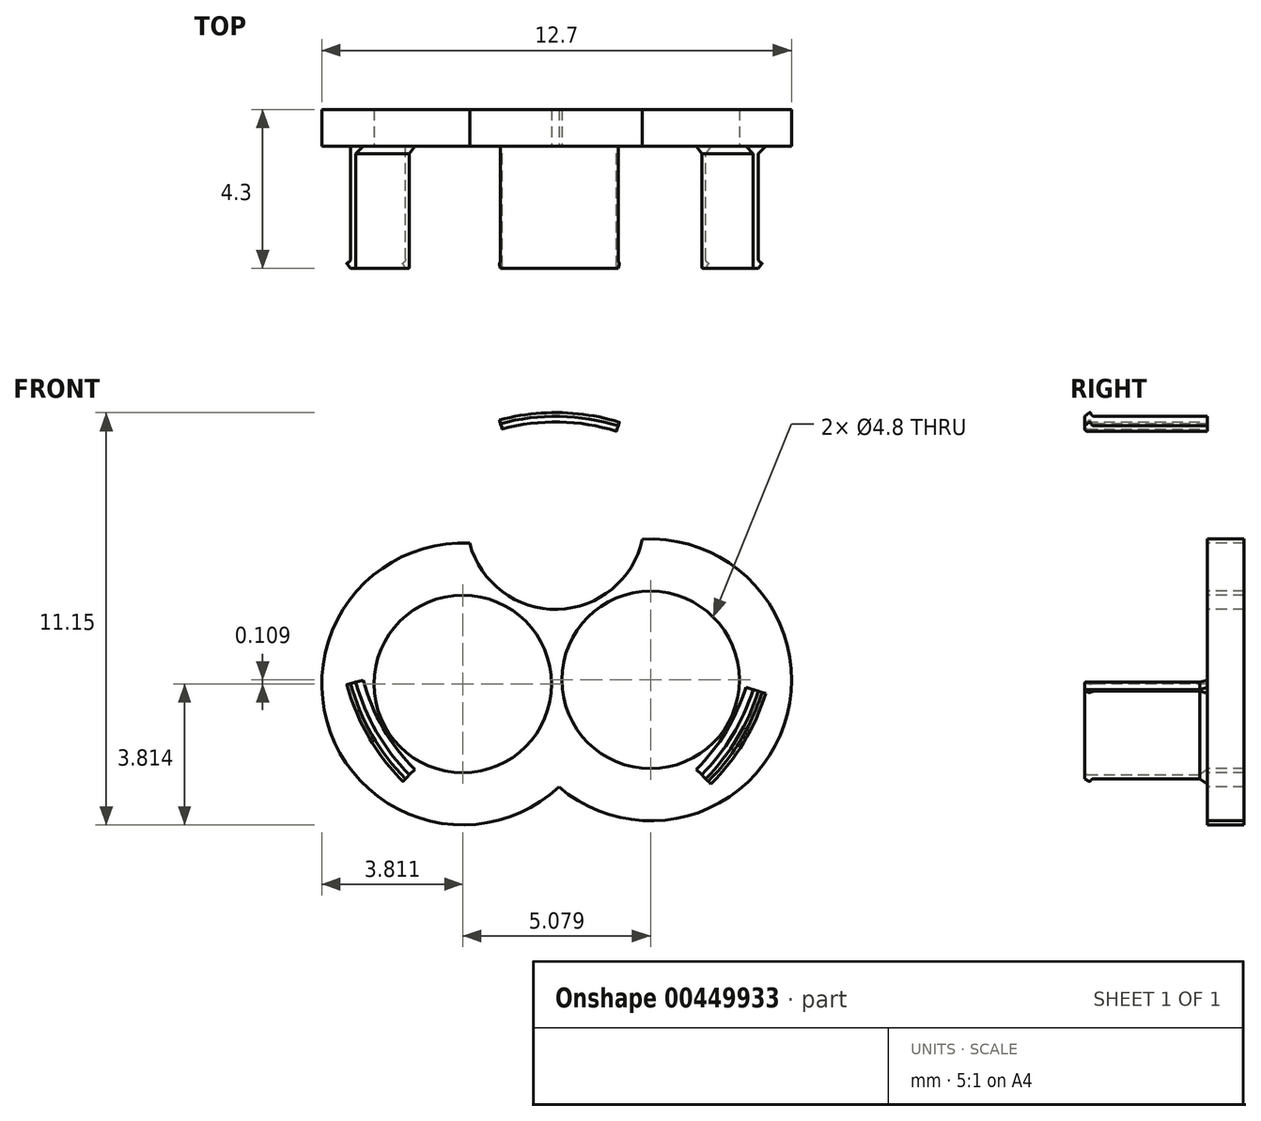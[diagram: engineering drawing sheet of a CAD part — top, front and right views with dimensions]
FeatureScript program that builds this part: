
annotation { "Feature Type Name" : "Feature", "Feature Type Description" : "" }
export const myFeature = defineFeature(function(context is Context, id is Id, definition is map)
    precondition{}
    {
        {
            var Q0;
            Q0=qCreatedBy(makeId("Front.planeOp"),FACE);
            var sketch = newSketch(context, id + "F0", { "sketchPlane" : qUnion([Q0])});
            skCircle(sketch, "E0", {"center": v(-2.5, -1.5) * mm, "radius": 2.4 * mm});
            skCircle(sketch, "E1", {"center": v(0, 2.92) * mm, "radius": 2.4 * mm});
            skCircle(sketch, "E2", {"center": v(0, 0) * mm, "radius": 2.92 * mm});
            skCircle(sketch, "E3", {"center": v(2.57, -1.39) * mm, "radius": 2.4 * mm});
            skCircle(sketch, "E4", {"center": v(-2.5, -1.5) * mm, "radius": 3.81 * mm});
            skCircle(sketch, "E5", {"center": v(0, 2.92) * mm, "radius": 3.81 * mm});
            skCircle(sketch, "E6", {"center": v(2.57, -1.39) * mm, "radius": 3.81 * mm});
            skSolve(sketch);
        }
        {
            var Q0;
            {var subQ0=sQuery(id+"F0.wireOp",EDGE,"E2");var subQ1=sQuery(id+"F0.wireOp",EDGE,"E0");var subQ2=makeQuery(id+"F0.imprint","INTERSECT",VERTEX,{"disambiguationData":[OD(0.0)],"derivedFrom":[subQ1,subQ0]});Q0=makeQuery(id+"F0.imprint","IMPRINT",FACE,{"disambiguationData":[TD([[makeQuery(id+"F0.imprint","IMPRINT",EDGE,{"disambiguationData":[TD([[subQ2,-1.0]])],"derivedFrom":subQ1}),-1.0]])]});}
            var Q1;
            {var subQ1=sQuery(id+"F0.wireOp",EDGE,"E2");var subQ5=sQuery(id+"F0.wireOp",EDGE,"E1");var subQ6=makeQuery(id+"F0.imprint","INTERSECT",VERTEX,{"disambiguationData":[OD(0.0)],"derivedFrom":[subQ5,subQ1]});Q1=makeQuery(id+"F0.imprint","IMPRINT",FACE,{"disambiguationData":[TD([[makeQuery(id+"F0.imprint","IMPRINT",EDGE,{"disambiguationData":[TD([[subQ6,-1.0]])],"derivedFrom":subQ5}),-1.0]])]});}
            var Q2;
            {var subQ5=sQuery(id+"F0.wireOp",EDGE,"E2");var subQ7=sQuery(id+"F0.wireOp",EDGE,"E1");var subQ9=makeQuery(id+"F0.imprint","INTERSECT",VERTEX,{"disambiguationData":[OD(0.0)],"derivedFrom":[subQ7,subQ5]});Q2=makeQuery(id+"F0.imprint","IMPRINT",FACE,{"disambiguationData":[TD([[makeQuery(id+"F0.imprint","IMPRINT",EDGE,{"disambiguationData":[TD([[subQ9,1.0]])],"derivedFrom":subQ7}),-1.0]])]});}
            var Q3;
            {var subQ1=sQuery(id+"F0.wireOp",EDGE,"E2");var subQ3=sQuery(id+"F0.wireOp",EDGE,"E0");var subQ5=makeQuery(id+"F0.imprint","INTERSECT",VERTEX,{"disambiguationData":[OD(0.0)],"derivedFrom":[subQ3,subQ1]});Q3=makeQuery(id+"F0.imprint","IMPRINT",FACE,{"disambiguationData":[TD([[makeQuery(id+"F0.imprint","IMPRINT",EDGE,{"disambiguationData":[TD([[subQ5,1.0]])],"derivedFrom":subQ3}),-1.0]])]});}
            var Q4;
            {var subQ0=sQuery(id+"F0.wireOp",EDGE,"E5");var subQ1=sQuery(id+"F0.wireOp",EDGE,"E0");var subQ2=makeQuery(id+"F0.imprint","INTERSECT",VERTEX,{"disambiguationData":[OD(1.0)],"derivedFrom":[subQ1,subQ0]});Q4=makeQuery(id+"F0.imprint","IMPRINT",FACE,{"disambiguationData":[TD([[makeQuery(id+"F0.imprint","IMPRINT",EDGE,{"disambiguationData":[TD([[subQ2,-1.0]])],"derivedFrom":subQ1}),-1.0]])]});}
            var Q5;
            {var subQ0=sQuery(id+"F0.wireOp",EDGE,"E6");var subQ5=sQuery(id+"F0.wireOp",EDGE,"E0");var subQ6=makeQuery(id+"F0.imprint","INTERSECT",VERTEX,{"disambiguationData":[OD(1.0)],"derivedFrom":[subQ5,subQ0]});Q5=makeQuery(id+"F0.imprint","IMPRINT",FACE,{"disambiguationData":[TD([[makeQuery(id+"F0.imprint","IMPRINT",EDGE,{"disambiguationData":[TD([[subQ6,-1.0]])],"derivedFrom":subQ5}),-1.0]])]});}
            var Q6;
            {var subQ0=sQuery(id+"F0.wireOp",EDGE,"E5");var subQ1=sQuery(id+"F0.wireOp",EDGE,"E3");var subQ2=makeQuery(id+"F0.imprint","INTERSECT",VERTEX,{"disambiguationData":[OD(0.0)],"derivedFrom":[subQ1,subQ0]});Q6=makeQuery(id+"F0.imprint","IMPRINT",FACE,{"disambiguationData":[TD([[makeQuery(id+"F0.imprint","IMPRINT",EDGE,{"disambiguationData":[TD([[subQ2,1.0]])],"derivedFrom":subQ1}),-1.0]])]});}
            var Q7;
            {var subQ0=sQuery(id+"F0.wireOp",EDGE,"E5");var subQ1=sQuery(id+"F0.wireOp",EDGE,"E0");var subQ2=makeQuery(id+"F0.imprint","INTERSECT",VERTEX,{"disambiguationData":[OD(0.0)],"derivedFrom":[subQ1,subQ0]});Q7=makeQuery(id+"F0.imprint","IMPRINT",FACE,{"disambiguationData":[TD([[makeQuery(id+"F0.imprint","IMPRINT",EDGE,{"disambiguationData":[TD([[subQ2,1.0]])],"derivedFrom":subQ1}),-1.0]])]});}
            var Q8;
            {var subQ7=sQuery(id+"F0.wireOp",EDGE,"E6");var subQ9=sQuery(id+"F0.wireOp",EDGE,"E0");var subQ10=makeQuery(id+"F0.imprint","INTERSECT",VERTEX,{"disambiguationData":[OD(0.0)],"derivedFrom":[subQ9,subQ7]});Q8=makeQuery(id+"F0.imprint","IMPRINT",FACE,{"disambiguationData":[TD([[makeQuery(id+"F0.imprint","IMPRINT",EDGE,{"disambiguationData":[TD([[subQ10,1.0]])],"derivedFrom":subQ9}),-1.0]])]});}
            var Q9;
            {var subQ1=sQuery(id+"F0.wireOp",EDGE,"E2");var subQ5=sQuery(id+"F0.wireOp",EDGE,"E1");var subQ6=makeQuery(id+"F0.imprint","INTERSECT",VERTEX,{"disambiguationData":[OD(1.0)],"derivedFrom":[subQ5,subQ1]});Q9=makeQuery(id+"F0.imprint","IMPRINT",FACE,{"disambiguationData":[TD([[makeQuery(id+"F0.imprint","IMPRINT",EDGE,{"disambiguationData":[TD([[subQ6,-1.0]])],"derivedFrom":subQ5}),-1.0]])]});}
            var Q10;
            {var subQ0=sQuery(id+"F0.wireOp",EDGE,"E4");var subQ1=sQuery(id+"F0.wireOp",EDGE,"E1");var subQ2=makeQuery(id+"F0.imprint","INTERSECT",VERTEX,{"disambiguationData":[OD(1.0)],"derivedFrom":[subQ1,subQ0]});Q10=makeQuery(id+"F0.imprint","IMPRINT",FACE,{"disambiguationData":[TD([[makeQuery(id+"F0.imprint","IMPRINT",EDGE,{"disambiguationData":[TD([[subQ2,-1.0]])],"derivedFrom":subQ1}),-1.0]])]});}
            var Q11;
            {var subQ0=sQuery(id+"F0.wireOp",EDGE,"E4");var subQ1=sQuery(id+"F0.wireOp",EDGE,"E1");var subQ2=makeQuery(id+"F0.imprint","INTERSECT",VERTEX,{"disambiguationData":[OD(0.0)],"derivedFrom":[subQ1,subQ0]});Q11=makeQuery(id+"F0.imprint","IMPRINT",FACE,{"disambiguationData":[TD([[makeQuery(id+"F0.imprint","IMPRINT",EDGE,{"disambiguationData":[TD([[subQ2,1.0]])],"derivedFrom":subQ1}),-1.0]])]});}
            extrude(context, id + "F1", {"entities" : qUnion([Q0, Q1, Q2, Q3, Q4, Q5, Q6, Q7, Q8, Q9, Q10, Q11]), "oppositeDirection" : true, "depth" : 1 * mm});
        }
        {
            var Q0;
            Q0=qCreatedBy(makeId("Right.planeOp"),FACE);
            var sketch = newSketch(context, id + "F2", { "sketchPlane" : qUnion([Q0])});
            skLineSegment(sketch, "E7", {"start": v(0, 5.59) * mm, "end": v(-3.25, 5.59) * mm});
            skLineSegment(sketch, "E8", {"start": v(-3.3, 5.64) * mm, "end": v(-3.3, 5.74) * mm});
            skLineSegment(sketch, "E9", {"start": v(-3.3, 5.74) * mm, "end": v(-3.15, 5.87) * mm});
            skLineSegment(sketch, "E10", {"start": v(-3.15, 5.87) * mm, "end": v(-3.15, 5.84) * mm});
            skLineSegment(sketch, "E11", {"start": v(-3.05, 5.74) * mm, "end": v(0, 5.74) * mm});
            skLineSegment(sketch, "E12", {"start": v(0, 5.74) * mm, "end": v(0, 5.59) * mm});
            skPoint(sketch, "E13.visualSharp", {"position": v(-3.3, 5.59) * mm});
            skArc(sketch, "E13.filletArc", {"start": v(-3.3, 5.64) * mm, "mid": v(-3.29, 5.6) * mm, "end": v(-3.25, 5.59) * mm});
            skPoint(sketch, "E14.visualSharp", {"position": v(-3.15, 5.74) * mm});
            skArc(sketch, "E14.filletArc", {"start": v(-3.15, 5.84) * mm, "mid": v(-3.12, 5.77) * mm, "end": v(-3.05, 5.74) * mm});
            skLineSegment(sketch, "E15", {"start": v(0, 0) * mm, "end": v(-3.26, 0) * mm});
            skSolve(sketch);
        }
        {
            var Q0;
            Q0=makeQuery(id+"F2.imprint","IMPRINT",FACE,{"disambiguationData":[TD([[makeQuery(id+"F2.imprint","IMPRINT",EDGE,{"derivedFrom":sQuery(id+"F2.wireOp",EDGE,"E7")}),-1.0]])]});
            var Q1;
            Q1=sQuery(id+"F2.wireOp",EDGE,"E15");
            revolve(context, id + "F3", {"operationType" : NewBodyOperationType.ADD, "entities" : qUnion([Q0]), "axis" : qUnion([Q1]), "revolveType" : RevolveType.FULL});
        }
        {
            var Q0;
            {var subQ0=sQuery(id+"F0.wireOp",EDGE,"E2");var subQ1=sQuery(id+"F0.wireOp",EDGE,"E1");var subQ2=sQuery(id+"F0.wireOp",EDGE,"E3");var subQ3=sQuery(id+"F0.wireOp",EDGE,"E0");var subQ4=sQuery(id+"F0.wireOp",EDGE,"E4");var subQ5=sQuery(id+"F0.wireOp",EDGE,"E5");var subQ6=sQuery(id+"F0.wireOp",EDGE,"E6");Q0=makeQuery(id+"F3.boolean.opBoolean","SPLIT",FACE,{"disambiguationData":[TD([makeQuery(id+"F1.opExtrude","SWEPT_FACE",FACE,{"disambiguationData":[OSD([subQ3])]}),makeQuery(id+"F1.opExtrude","SWEPT_FACE",FACE,{"disambiguationData":[OSD([subQ1])]}),makeQuery(id+"F1.opExtrude","SWEPT_FACE",FACE,{"disambiguationData":[OSD([subQ0])]}),makeQuery(id+"F1.opExtrude","SWEPT_FACE",FACE,{"disambiguationData":[OSD([subQ2])]}),makeQuery(id+"F1.opExtrude","SWEPT_FACE",FACE,{"disambiguationData":[OSD([subQ4])]}),makeQuery(id+"F1.opExtrude","SWEPT_FACE",FACE,{"disambiguationData":[OSD([subQ5])]}),makeQuery(id+"F1.opExtrude","SWEPT_FACE",FACE,{"disambiguationData":[OSD([subQ6])]}),makeQuery(id+"F3.opRevolve","SWEPT_FACE",FACE,{"disambiguationData":[OSD([sQuery(id+"F2.wireOp",EDGE,"E7")])]}),makeQuery(id+"F3.opRevolve","SWEPT_FACE",FACE,{"disambiguationData":[OSD([sQuery(id+"F2.wireOp",EDGE,"E12")])]})])],"derivedFrom":makeQuery(id+"F1.opExtrude","CAP_FACE",FACE,{"disambiguationData":[OSD([subQ3,subQ1,subQ0,subQ2,subQ4,subQ5,subQ6])],"isStart":true})});}
            var sketch = newSketch(context, id + "F4", { "sketchPlane" : qUnion([Q0])});
            skLineSegment(sketch, "E16", {"start": v(-12.27, -3.29) * mm, "end": v(0, 0) * mm});
            skLineSegment(sketch, "E17", {"start": v(0, 0) * mm, "end": v(-8.98, -8.98) * mm});
            skLineSegment(sketch, "E18", {"start": v(-8.98, -8.98) * mm, "end": v(8.98, -8.98) * mm});
            skLineSegment(sketch, "E19", {"start": v(8.98, -8.98) * mm, "end": v(0, 0) * mm});
            skLineSegment(sketch, "E20", {"start": v(0, 0) * mm, "end": v(12.13, -3.75) * mm});
            skLineSegment(sketch, "E21", {"start": v(12.13, -3.75) * mm, "end": v(3.75, 12.13) * mm});
            skLineSegment(sketch, "E22", {"start": v(3.75, 12.13) * mm, "end": v(0, 0) * mm});
            skLineSegment(sketch, "E23", {"start": v(0, 0) * mm, "end": v(-3.29, 12.27) * mm});
            skLineSegment(sketch, "E24", {"start": v(-3.29, 12.27) * mm, "end": v(-12.27, -3.29) * mm});
            skSolve(sketch);
        }
        {
            var Q0;
            Q0 = qSketchRegion(id + "F4", true);
            extrude(context, id + "F5", {"entities" : qUnion([Q0]), "operationType" : NewBodyOperationType.REMOVE, "depth" : 25.4 * mm});
        }
        {
            var Q0;
            {var subQ0=sQuery(id+"F0.wireOp",EDGE,"E6");var subQ1=makeQuery(id+"F1.opExtrude","CAP_FACE",FACE,{"disambiguationData":[OSD([sQuery(id+"F0.wireOp",EDGE,"E0"),sQuery(id+"F0.wireOp",EDGE,"E1"),sQuery(id+"F0.wireOp",EDGE,"E3"),sQuery(id+"F0.wireOp",EDGE,"E4"),sQuery(id+"F0.wireOp",EDGE,"E5"),subQ0])],"isStart":true});var subQ2=sQuery(id+"F2.wireOp",EDGE,"E11");var subQ3=makeQuery(id+"F3.opRevolve","SWEPT_FACE",FACE,{"disambiguationData":[OSD([subQ2])]});var subQ4=sQuery(id+"F2.wireOp",EDGE,"E12");Q0=makeQuery(id+"F3.boolean.opBoolean","SPLIT",EDGE,{"disambiguationData":[topologyDisambiguationEdgeConnected([subQ1,subQ3]),TD([makeQuery(id+"F1.opExtrude","SWEPT_FACE",FACE,{"disambiguationData":[OSD([subQ0])]})])],"derivedFrom":makeQuery(id+"F3.opRevolve","SWEPT_EDGE",EDGE,{"disambiguationData":[OSD([subQ2,subQ4])]})});}
            var Q1;
            {var subQ0=sQuery(id+"F0.wireOp",EDGE,"E6");var subQ1=makeQuery(id+"F1.opExtrude","CAP_FACE",FACE,{"disambiguationData":[OSD([sQuery(id+"F0.wireOp",EDGE,"E0"),sQuery(id+"F0.wireOp",EDGE,"E1"),sQuery(id+"F0.wireOp",EDGE,"E3"),sQuery(id+"F0.wireOp",EDGE,"E4"),sQuery(id+"F0.wireOp",EDGE,"E5"),subQ0])],"isStart":true});var subQ2=sQuery(id+"F2.wireOp",EDGE,"E7");var subQ3=makeQuery(id+"F3.opRevolve","SWEPT_FACE",FACE,{"disambiguationData":[OSD([subQ2])]});var subQ4=sQuery(id+"F2.wireOp",EDGE,"E12");Q1=makeQuery(id+"F3.boolean.opBoolean","SPLIT",EDGE,{"disambiguationData":[topologyDisambiguationEdgeConnected([subQ1,subQ3]),TD([makeQuery(id+"F1.opExtrude","SWEPT_FACE",FACE,{"disambiguationData":[OSD([subQ0])]})])],"derivedFrom":makeQuery(id+"F3.opRevolve","SWEPT_EDGE",EDGE,{"disambiguationData":[OSD([subQ2,subQ4])]})});}
            var Q2;
            {var subQ0=sQuery(id+"F0.wireOp",EDGE,"E4");var subQ1=makeQuery(id+"F1.opExtrude","CAP_FACE",FACE,{"disambiguationData":[OSD([sQuery(id+"F0.wireOp",EDGE,"E0"),sQuery(id+"F0.wireOp",EDGE,"E1"),sQuery(id+"F0.wireOp",EDGE,"E3"),subQ0,sQuery(id+"F0.wireOp",EDGE,"E5"),sQuery(id+"F0.wireOp",EDGE,"E6")])],"isStart":true});var subQ2=sQuery(id+"F2.wireOp",EDGE,"E11");var subQ3=makeQuery(id+"F3.opRevolve","SWEPT_FACE",FACE,{"disambiguationData":[OSD([subQ2])]});var subQ4=sQuery(id+"F2.wireOp",EDGE,"E12");Q2=makeQuery(id+"F3.boolean.opBoolean","SPLIT",EDGE,{"disambiguationData":[topologyDisambiguationEdgeConnected([subQ1,subQ3]),TD([makeQuery(id+"F1.opExtrude","SWEPT_FACE",FACE,{"disambiguationData":[OSD([subQ0])]})])],"derivedFrom":makeQuery(id+"F3.opRevolve","SWEPT_EDGE",EDGE,{"disambiguationData":[OSD([subQ2,subQ4])]})});}
            var Q3;
            {var subQ0=sQuery(id+"F0.wireOp",EDGE,"E5");var subQ1=makeQuery(id+"F1.opExtrude","CAP_FACE",FACE,{"disambiguationData":[OSD([sQuery(id+"F0.wireOp",EDGE,"E0"),sQuery(id+"F0.wireOp",EDGE,"E1"),sQuery(id+"F0.wireOp",EDGE,"E3"),sQuery(id+"F0.wireOp",EDGE,"E4"),subQ0,sQuery(id+"F0.wireOp",EDGE,"E6")])],"isStart":true});var subQ2=sQuery(id+"F2.wireOp",EDGE,"E7");var subQ3=makeQuery(id+"F3.opRevolve","SWEPT_FACE",FACE,{"disambiguationData":[OSD([subQ2])]});var subQ4=sQuery(id+"F2.wireOp",EDGE,"E12");Q3=makeQuery(id+"F3.boolean.opBoolean","SPLIT",EDGE,{"disambiguationData":[topologyDisambiguationEdgeConnected([subQ1,subQ3]),TD([makeQuery(id+"F1.opExtrude","SWEPT_FACE",FACE,{"disambiguationData":[OSD([subQ0])]})])],"derivedFrom":makeQuery(id+"F3.opRevolve","SWEPT_EDGE",EDGE,{"disambiguationData":[OSD([subQ2,subQ4])]})});}
            var Q4;
            {var subQ0=sQuery(id+"F0.wireOp",EDGE,"E5");var subQ1=makeQuery(id+"F1.opExtrude","CAP_FACE",FACE,{"disambiguationData":[OSD([sQuery(id+"F0.wireOp",EDGE,"E0"),sQuery(id+"F0.wireOp",EDGE,"E1"),sQuery(id+"F0.wireOp",EDGE,"E3"),sQuery(id+"F0.wireOp",EDGE,"E4"),subQ0,sQuery(id+"F0.wireOp",EDGE,"E6")])],"isStart":true});var subQ2=sQuery(id+"F2.wireOp",EDGE,"E11");var subQ3=makeQuery(id+"F3.opRevolve","SWEPT_FACE",FACE,{"disambiguationData":[OSD([subQ2])]});var subQ4=sQuery(id+"F2.wireOp",EDGE,"E12");Q4=makeQuery(id+"F3.boolean.opBoolean","SPLIT",EDGE,{"disambiguationData":[topologyDisambiguationEdgeConnected([subQ1,subQ3]),TD([makeQuery(id+"F1.opExtrude","SWEPT_FACE",FACE,{"disambiguationData":[OSD([subQ0])]})])],"derivedFrom":makeQuery(id+"F3.opRevolve","SWEPT_EDGE",EDGE,{"disambiguationData":[OSD([subQ2,subQ4])]})});}
            var Q5;
            {var subQ0=sQuery(id+"F0.wireOp",EDGE,"E4");var subQ1=makeQuery(id+"F1.opExtrude","CAP_FACE",FACE,{"disambiguationData":[OSD([sQuery(id+"F0.wireOp",EDGE,"E0"),sQuery(id+"F0.wireOp",EDGE,"E1"),sQuery(id+"F0.wireOp",EDGE,"E3"),subQ0,sQuery(id+"F0.wireOp",EDGE,"E5"),sQuery(id+"F0.wireOp",EDGE,"E6")])],"isStart":true});var subQ2=sQuery(id+"F2.wireOp",EDGE,"E7");var subQ3=makeQuery(id+"F3.opRevolve","SWEPT_FACE",FACE,{"disambiguationData":[OSD([subQ2])]});var subQ4=sQuery(id+"F2.wireOp",EDGE,"E12");Q5=makeQuery(id+"F3.boolean.opBoolean","SPLIT",EDGE,{"disambiguationData":[topologyDisambiguationEdgeConnected([subQ1,subQ3]),TD([makeQuery(id+"F1.opExtrude","SWEPT_FACE",FACE,{"disambiguationData":[OSD([subQ0])]})])],"derivedFrom":makeQuery(id+"F3.opRevolve","SWEPT_EDGE",EDGE,{"disambiguationData":[OSD([subQ2,subQ4])]})});}
            chamfer(context, id + "F6", {"entities" : qUnion([Q0, Q1, Q2, Q3, Q4, Q5]), "width" : 0.2 * mm, "tangentPropagation" : true});
        }
        {
            var Q0;
            {var subQ0=sQuery(id+"F2.wireOp",EDGE,"E9");var subQ1=sQuery(id+"F2.wireOp",EDGE,"E10");Q0=makeQuery(id+"F5.boolean.opBoolean","SPLIT",EDGE,{"disambiguationData":[TD([makeQuery(id+"F5.opExtrude","SWEPT_FACE",FACE,{"disambiguationData":[OSD([sQuery(id+"F4.wireOp",EDGE,"E22")])]})])],"derivedFrom":makeQuery(id+"F3.opRevolve","SWEPT_EDGE",EDGE,{"disambiguationData":[OSD([subQ0,subQ1])]})});}
            var Q1;
            {var subQ0=sQuery(id+"F2.wireOp",EDGE,"E9");var subQ1=sQuery(id+"F2.wireOp",EDGE,"E10");Q1=makeQuery(id+"F5.boolean.opBoolean","SPLIT",EDGE,{"disambiguationData":[TD([makeQuery(id+"F5.opExtrude","SWEPT_FACE",FACE,{"disambiguationData":[OSD([sQuery(id+"F4.wireOp",EDGE,"E16")])]})])],"derivedFrom":makeQuery(id+"F3.opRevolve","SWEPT_EDGE",EDGE,{"disambiguationData":[OSD([subQ0,subQ1])]})});}
            var Q2;
            {var subQ0=sQuery(id+"F2.wireOp",EDGE,"E9");var subQ1=sQuery(id+"F2.wireOp",EDGE,"E10");Q2=makeQuery(id+"F5.boolean.opBoolean","SPLIT",EDGE,{"disambiguationData":[TD([makeQuery(id+"F5.opExtrude","SWEPT_FACE",FACE,{"disambiguationData":[OSD([sQuery(id+"F4.wireOp",EDGE,"E19")])]})])],"derivedFrom":makeQuery(id+"F3.opRevolve","SWEPT_EDGE",EDGE,{"disambiguationData":[OSD([subQ0,subQ1])]})});}
            fillet(context, id + "F7", {"entities" : qUnion([Q0, Q1, Q2]), "radius" : 0.03 * mm, "tangentPropagation" : true, "allowEdgeOverflow" : false});
        }
    });
